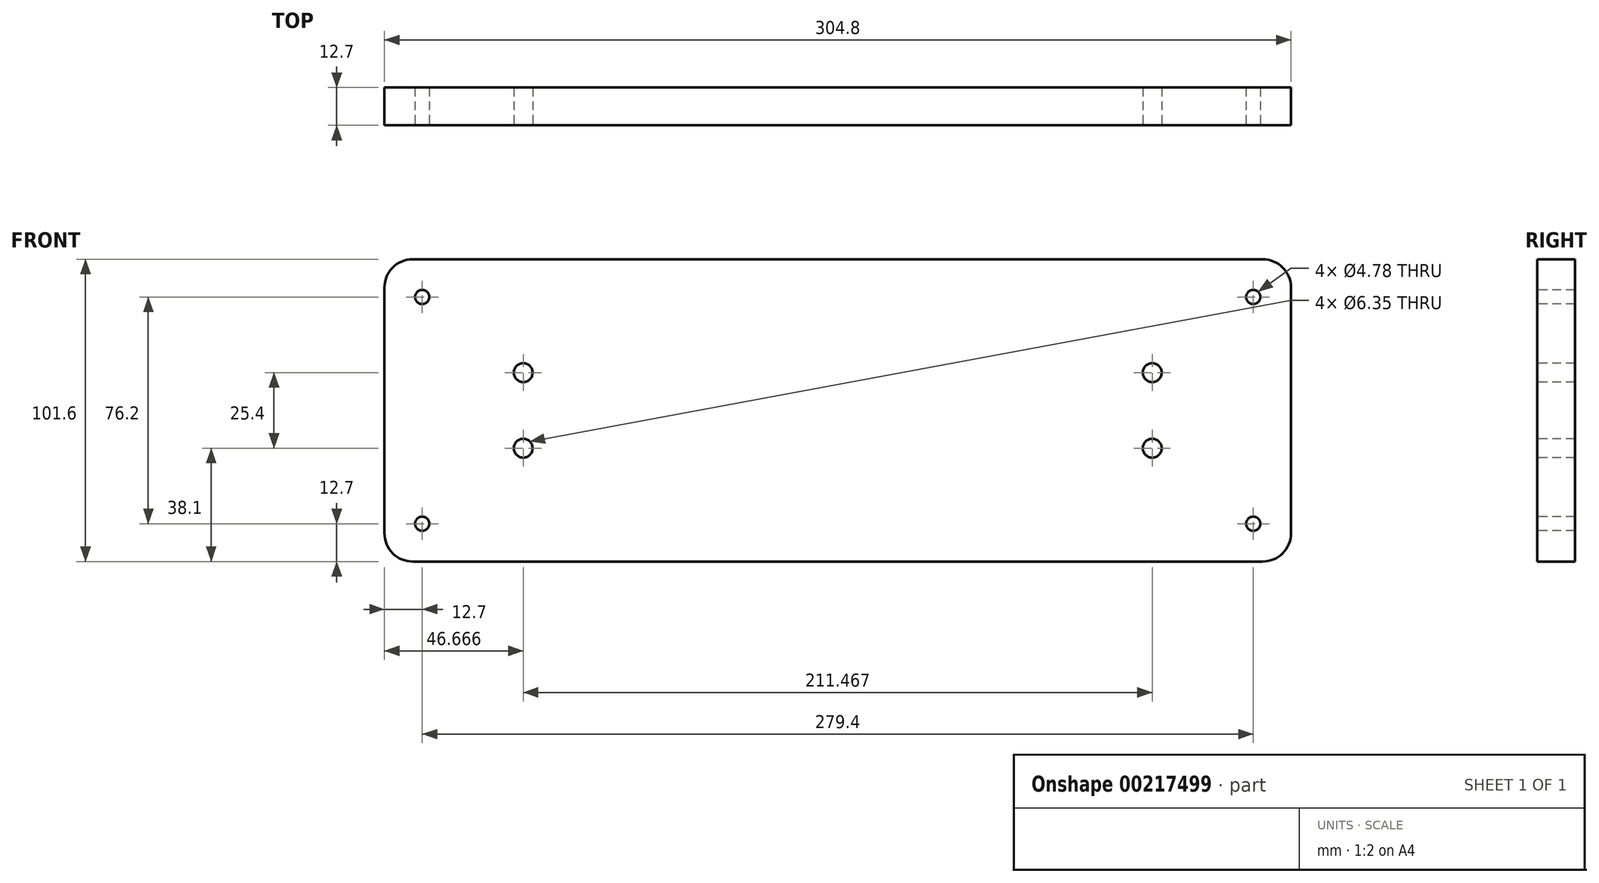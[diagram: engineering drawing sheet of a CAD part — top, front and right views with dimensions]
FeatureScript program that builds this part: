
annotation { "Feature Type Name" : "Feature", "Feature Type Description" : "" }
export const myFeature = defineFeature(function(context is Context, id is Id, definition is map)
    precondition{}
    {
        {
            var Q0;
            Q0=qCreatedBy(makeId("Front.planeOp"),FACE);
            var sketch = newSketch(context, id + "F0", { "sketchPlane" : qUnion([Q0])});
            skLineSegment(sketch, "E0.bottom", {"start": v(0, 0) * mm, "end": v(304.8, 0) * mm});
            skLineSegment(sketch, "E0.top", {"start": v(0, 101.6) * mm, "end": v(304.8, 101.6) * mm});
            skLineSegment(sketch, "E0.left", {"start": v(0, 0) * mm, "end": v(0, 101.6) * mm});
            skLineSegment(sketch, "E0.right", {"start": v(304.8, 0) * mm, "end": v(304.8, 101.6) * mm});
            skSolve(sketch);
        }
        {
            var Q0;
            Q0 = qSketchRegion(id + "F0", true);
            extrude(context, id + "F1", {"entities" : qUnion([Q0]), "depth" : 12.7 * mm});
        }
        {
            var Q0;
            Q0=makeQuery(id+"F1.opExtrude","SWEPT_EDGE",EDGE,{"disambiguationData":[OSD([sQuery(id+"F0.wireOp",EDGE,"E0.top"),sQuery(id+"F0.wireOp",EDGE,"E0.left")])]});
            var Q1;
            Q1=makeQuery(id+"F1.opExtrude","SWEPT_EDGE",EDGE,{"disambiguationData":[OSD([sQuery(id+"F0.wireOp",EDGE,"E0.top"),sQuery(id+"F0.wireOp",EDGE,"E0.right")])]});
            var Q2;
            Q2=makeQuery(id+"F1.opExtrude","SWEPT_EDGE",EDGE,{"disambiguationData":[OSD([sQuery(id+"F0.wireOp",EDGE,"E0.bottom"),sQuery(id+"F0.wireOp",EDGE,"E0.right")])]});
            var Q3;
            Q3=makeQuery(id+"F1.opExtrude","SWEPT_EDGE",EDGE,{"disambiguationData":[OSD([sQuery(id+"F0.wireOp",EDGE,"E0.bottom"),sQuery(id+"F0.wireOp",EDGE,"E0.left")])]});
            fillet(context, id + "F2", {"entities" : qUnion([Q0, Q1, Q2, Q3]), "radius" : 9.52 * mm, "tangentPropagation" : true, "allowEdgeOverflow" : false});
        }
        {
            var Q0;
            Q0=makeQuery(id+"F1.opExtrude","CAP_FACE",FACE,{"disambiguationData":[OSD([sQuery(id+"F0.wireOp",EDGE,"E0.bottom"),sQuery(id+"F0.wireOp",EDGE,"E0.top"),sQuery(id+"F0.wireOp",EDGE,"E0.left"),sQuery(id+"F0.wireOp",EDGE,"E0.right")])],"isStart":false});
            var sketch = newSketch(context, id + "F3", { "sketchPlane" : qUnion([Q0])});
            skPoint(sketch, "E1", {"position": v(12.7, 88.9) * mm});
            skPoint(sketch, "E2", {"position": v(12.7, 12.7) * mm});
            skPoint(sketch, "E3", {"position": v(292.1, 88.9) * mm});
            skPoint(sketch, "E4", {"position": v(292.1, 12.7) * mm});
            skSolve(sketch);
        }
        {
            var Q0;
            Q0=sQuery(id+"F3.wireOp",VERTEX,"E1");
            var Q1;
            Q1=sQuery(id+"F3.wireOp",VERTEX,"E2");
            var Q2;
            Q2=sQuery(id+"F3.wireOp",VERTEX,"E4");
            var Q3;
            Q3=sQuery(id+"F3.wireOp",VERTEX,"E3");
            var Q4;
            Q4=makeQuery(id+"F1.opExtrude","SWEPT_BODY",BODY,{"disambiguationData":[OSD([sQuery(id+"F0.wireOp",EDGE,"E0.bottom"),sQuery(id+"F0.wireOp",EDGE,"E0.top"),sQuery(id+"F0.wireOp",EDGE,"E0.left"),sQuery(id+"F0.wireOp",EDGE,"E0.right")])]});
            hole(context, id + "F4", {"style" : HoleStyle.SIMPLE, "endStyle" : HoleEndStyle.THROUGH, "holeDiameter" : 4.78 * mm, "locations" : qUnion([Q0, Q1, Q2, Q3]), "scope" : qUnion([Q4]), "isTappedThrough" : true});
        }
        {
            var Q0;
            Q0=makeQuery(id+"F1.opExtrude","CAP_FACE",FACE,{"disambiguationData":[OSD([sQuery(id+"F0.wireOp",EDGE,"E0.bottom"),sQuery(id+"F0.wireOp",EDGE,"E0.top"),sQuery(id+"F0.wireOp",EDGE,"E0.left"),sQuery(id+"F0.wireOp",EDGE,"E0.right")])],"isStart":false});
            var sketch = newSketch(context, id + "F5", { "sketchPlane" : qUnion([Q0])});
            skPoint(sketch, "E5", {"position": v(46.67, 63.5) * mm});
            skPoint(sketch, "E6.MirrorP", {"position": v(46.67, 38.1) * mm});
            skPoint(sketch, "E7.MirrorP", {"position": v(258.13, 63.5) * mm});
            skPoint(sketch, "E8.MirrorP", {"position": v(258.13, 38.1) * mm});
            skSolve(sketch);
        }
        {
            var Q0;
            Q0=sQuery(id+"F5.wireOp",VERTEX,"E5");
            var Q1;
            Q1=sQuery(id+"F5.wireOp",VERTEX,"E6.MirrorP");
            var Q2;
            Q2=sQuery(id+"F5.wireOp",VERTEX,"E7.MirrorP");
            var Q3;
            Q3=sQuery(id+"F5.wireOp",VERTEX,"E8.MirrorP");
            var Q4;
            Q4=makeQuery(id+"F1.opExtrude","SWEPT_BODY",BODY,{"disambiguationData":[OSD([sQuery(id+"F0.wireOp",EDGE,"E0.bottom"),sQuery(id+"F0.wireOp",EDGE,"E0.top"),sQuery(id+"F0.wireOp",EDGE,"E0.left"),sQuery(id+"F0.wireOp",EDGE,"E0.right")])]});
            hole(context, id + "F6", {"style" : HoleStyle.SIMPLE, "endStyle" : HoleEndStyle.THROUGH, "holeDiameter" : 6.35 * mm, "locations" : qUnion([Q0, Q1, Q2, Q3]), "scope" : qUnion([Q4]), "isTappedThrough" : true});
        }
    });
